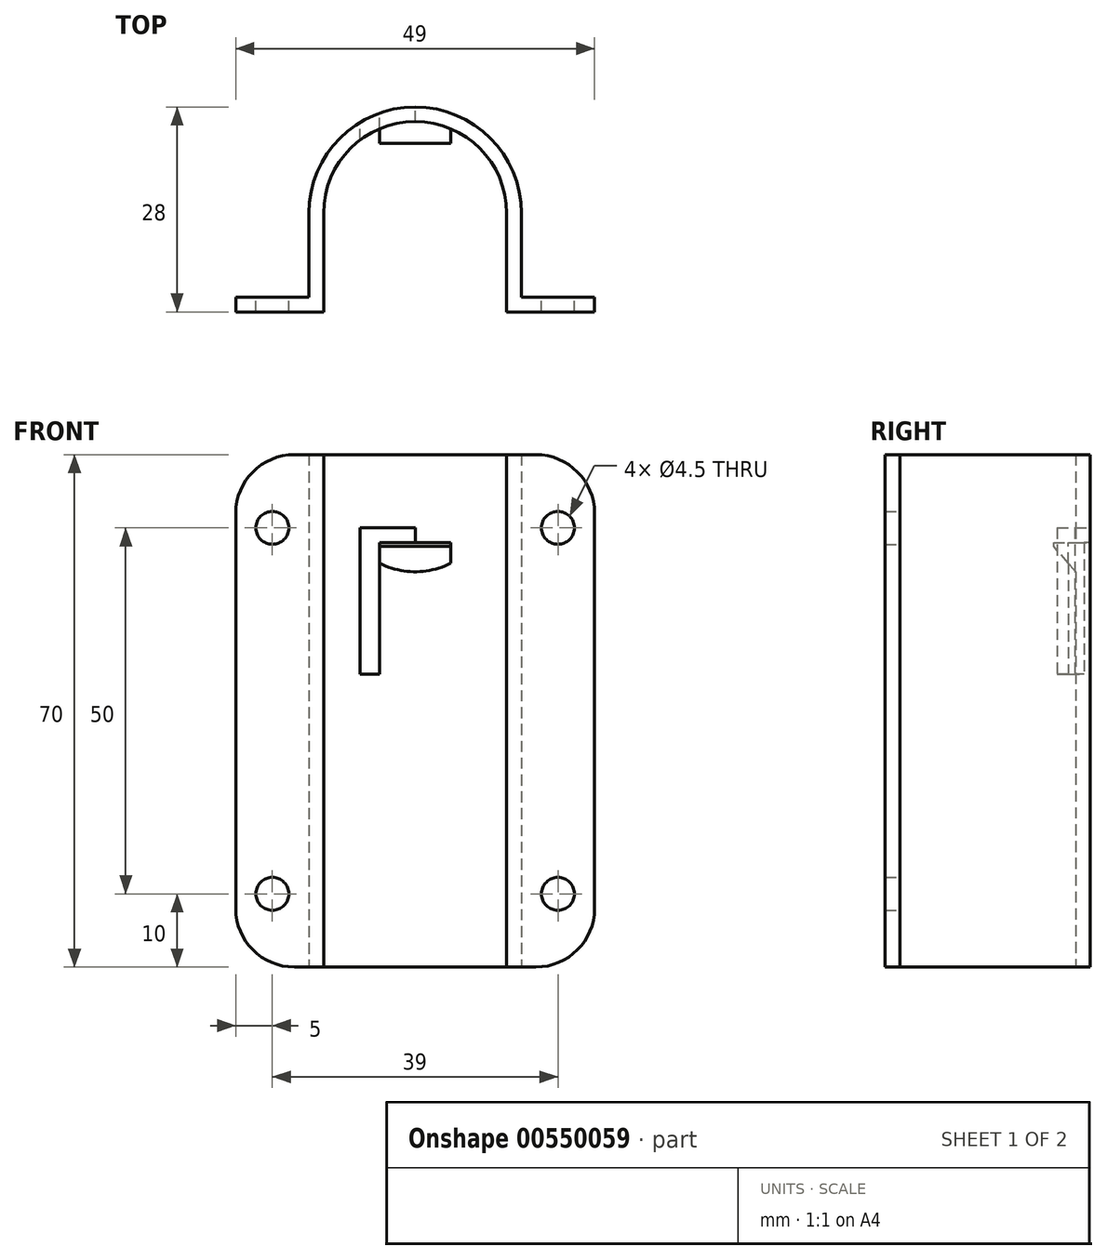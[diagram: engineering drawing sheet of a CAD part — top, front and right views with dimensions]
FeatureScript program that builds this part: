
annotation { "Feature Type Name" : "Feature", "Feature Type Description" : "" }
export const myFeature = defineFeature(function(context is Context, id is Id, definition is map)
    precondition{}
    {
        {
            var Q0;
            Q0=qCreatedBy(makeId("Top.planeOp"),FACE);
            var sketch = newSketch(context, id + "F0", { "sketchPlane" : qUnion([Q0])});
            skLineSegment(sketch, "E0", {"start": v(-24.5, 0) * mm, "end": v(-24.5, 2) * mm});
            skLineSegment(sketch, "E1", {"start": v(-24.5, 2) * mm, "end": v(-14.5, 2) * mm});
            skLineSegment(sketch, "E2", {"start": v(-14.5, 2) * mm, "end": v(-14.5, 13.5) * mm});
            skArc(sketch, "E3", {"start": v(-14.5, 13.5) * mm, "mid": v(-10.25, 23.75) * mm, "end": v(0, 28) * mm});
            skLineSegment(sketch, "E4", {"start": v(0, 28) * mm, "end": v(0, 26) * mm});
            skArc(sketch, "E5", {"start": v(0, 26) * mm, "mid": v(-8.84, 22.34) * mm, "end": v(-12.5, 13.5) * mm});
            skLineSegment(sketch, "E6", {"start": v(-12.5, 13.5) * mm, "end": v(-12.5, 0) * mm});
            skLineSegment(sketch, "E7", {"start": v(-24.5, 0) * mm, "end": v(-12.5, 0) * mm});
            skSolve(sketch);
        }
        {
            var Q0;
            Q0=makeQuery(id+"F0.imprint","IMPRINT",FACE,{"disambiguationData":[TD([[makeQuery(id+"F0.imprint","IMPRINT",EDGE,{"derivedFrom":sQuery(id+"F0.wireOp",EDGE,"E0")}),-1.0]])]});
            extrude(context, id + "F1", {"entities" : qUnion([Q0]), "endBound" : BoundingType.SYMMETRIC, "depth" : 70 * mm, "offsetDistance" : 25 * mm});
        }
        {
            var Q0;
            Q0=makeQuery(id+"F1.opExtrude","SWEPT_FACE",FACE,{"disambiguationData":[OSD([sQuery(id+"F0.wireOp",EDGE,"E1")])]});
            var sketch = newSketch(context, id + "F2", { "sketchPlane" : qUnion([Q0])});
            skPoint(sketch, "E8", {"position": v(19.5, 25) * mm});
            skPoint(sketch, "E9", {"position": v(19.5, -25) * mm});
            skSolve(sketch);
        }
        {
            var Q0;
            Q0=sQuery(id+"F2.wireOp",VERTEX,"E9");
            var Q1;
            Q1=sQuery(id+"F2.wireOp",VERTEX,"E8");
            var Q2;
            Q2=makeQuery(id+"F1.opExtrude","SWEPT_BODY",BODY,{"disambiguationData":[OSD([sQuery(id+"F0.wireOp",EDGE,"E0"),sQuery(id+"F0.wireOp",EDGE,"E1"),sQuery(id+"F0.wireOp",EDGE,"E2"),sQuery(id+"F0.wireOp",EDGE,"E3"),sQuery(id+"F0.wireOp",EDGE,"E4"),sQuery(id+"F0.wireOp",EDGE,"E5"),sQuery(id+"F0.wireOp",EDGE,"E6"),sQuery(id+"F0.wireOp",EDGE,"E7")])]});
            hole(context, id + "F3", {"style" : HoleStyle.SIMPLE, "endStyle" : HoleEndStyle.THROUGH, "holeDiameter" : 4.5 * mm, "isTappedThrough" : true, "tappedDepth" : 12 * mm, "tapClearance" : 3, "locations" : qUnion([Q0, Q1]), "scope" : qUnion([Q2])});
        }
        {
            var Q0;
            Q0=makeQuery(id+"F1.opExtrude","SWEPT_BODY",BODY,{"disambiguationData":[OSD([sQuery(id+"F0.wireOp",EDGE,"E0"),sQuery(id+"F0.wireOp",EDGE,"E1"),sQuery(id+"F0.wireOp",EDGE,"E2"),sQuery(id+"F0.wireOp",EDGE,"E3"),sQuery(id+"F0.wireOp",EDGE,"E4"),sQuery(id+"F0.wireOp",EDGE,"E5"),sQuery(id+"F0.wireOp",EDGE,"E6"),sQuery(id+"F0.wireOp",EDGE,"E7")])]});
            var Q1;
            Q1=qCreatedBy(makeId("Right.planeOp"),FACE);
            mirror(context, id + "F4", {"operationType" : NewBodyOperationType.ADD, "entities" : qUnion([Q0]), "mirrorPlane" : qUnion([Q1])});
        }
        {
            var Q0;
            Q0=qCreatedBy(makeId("Front.planeOp"),FACE);
            cPlane(context, id + "F5", {"entities" : qUnion([Q0]), "cplaneType" : CPlaneType.OFFSET, "offset" : 29 * mm, "oppositeDirection" : true, "width" : 150 * mm, "height" : 150 * mm});
        }
        {
            var Q0;
            Q0=qCreatedBy(id+"F5.planeOp",FACE);
            var sketch = newSketch(context, id + "F6", { "sketchPlane" : qUnion([Q0])});
            skLineSegment(sketch, "E10", {"start": v(0, 25) * mm, "end": v(-7.5, 25) * mm});
            skLineSegment(sketch, "E11", {"start": v(-7.5, 25) * mm, "end": v(-7.5, 5) * mm});
            skLineSegment(sketch, "E12", {"start": v(-7.5, 5) * mm, "end": v(-4.89, 5) * mm});
            skLineSegment(sketch, "E13", {"start": v(-4.89, 5) * mm, "end": v(-4.89, 23) * mm});
            skLineSegment(sketch, "E14", {"start": v(-4.89, 23) * mm, "end": v(0, 23) * mm});
            skLineSegment(sketch, "E15", {"start": v(0, 23) * mm, "end": v(0, 25) * mm});
            skSolve(sketch);
        }
        {
            var Q0;
            Q0=makeQuery(id+"F6.imprint","IMPRINT",FACE,{"disambiguationData":[TD([[makeQuery(id+"F6.imprint","IMPRINT",EDGE,{"derivedFrom":sQuery(id+"F6.wireOp",EDGE,"E10")}),1.0]])]});
            var Q1;
            {var subQ0=makeQuery(id+"F1.opExtrude","SWEPT_FACE",FACE,{"disambiguationData":[OSD([sQuery(id+"F0.wireOp",EDGE,"E5")])]});Q1=makeQuery(id+"F4.boolean.opBoolean","MERGE",FACE,{"derivedFrom":[subQ0,makeQuery(id+"F4.opPattern","COPY",FACE,{"derivedFrom":subQ0,"instanceName":"1"})]});}
            extrude(context, id + "F7", {"entities" : qUnion([Q0]), "operationType" : NewBodyOperationType.REMOVE, "endBound" : BoundingType.UP_TO_SURFACE, "depth" : 25 * mm, "endBoundEntityFace" : qUnion([Q1]), "offsetDistance" : 25 * mm});
        }
        {
            var Q0;
            Q0=makeQuery(id+"F1.opExtrude","CAP_EDGE",EDGE,{"disambiguationData":[OSD([sQuery(id+"F0.wireOp",EDGE,"E0")])],"isStart":true});
            var Q1;
            Q1=makeQuery(id+"F4.opPattern","COPY",EDGE,{"derivedFrom":makeQuery(id+"F1.opExtrude","CAP_EDGE",EDGE,{"disambiguationData":[OSD([sQuery(id+"F0.wireOp",EDGE,"E0")])],"isStart":true}),"instanceName":"1"});
            var Q2;
            Q2=makeQuery(id+"F1.opExtrude","CAP_EDGE",EDGE,{"disambiguationData":[OSD([sQuery(id+"F0.wireOp",EDGE,"E0")])],"isStart":false});
            var Q3;
            Q3=makeQuery(id+"F4.opPattern","COPY",EDGE,{"derivedFrom":makeQuery(id+"F1.opExtrude","CAP_EDGE",EDGE,{"disambiguationData":[OSD([sQuery(id+"F0.wireOp",EDGE,"E0")])],"isStart":false}),"instanceName":"1"});
            fillet(context, id + "F8", {"entities" : qUnion([Q0, Q1, Q2, Q3]), "radius" : 8 * mm, "tangentPropagation" : true, "allowEdgeOverflow" : false});
        }
        {
            var Q0;
            {var subQ0=sQuery(id+"F6.wireOp",EDGE,"E14");Q0=makeQuery(id+"FHmU98y3rWXlE6b_1.1.F7.boolean.opBoolean","MERGE",FACE,{"derivedFrom":[makeQuery(id+"F7.boolean.opBoolean","COPY",FACE,{"derivedFrom":makeQuery(id+"F7.opExtrude","SWEPT_FACE",FACE,{"disambiguationData":[OSD([subQ0])]})}),makeQuery(id+"FHmU98y3rWXlE6b_1.1.F7.opExtrude","SWEPT_FACE",FACE,{"disambiguationData":[OSD([subQ0])]})]});}
            var sketch = newSketch(context, id + "F9", { "sketchPlane" : qUnion([Q0])});
            skLineSegment(sketch, "E16", {"start": v(-4.89, 25) * mm, "end": v(-4.89, 23) * mm});
            skLineSegment(sketch, "E17", {"start": v(-4.89, 23) * mm, "end": v(4.89, 23) * mm});
            skLineSegment(sketch, "E18", {"start": v(4.89, 23) * mm, "end": v(4.89, 25) * mm});
            skArc(sketch, "E19", {"start": v(4.89, 25) * mm, "mid": v(0, 26) * mm, "end": v(-4.89, 25) * mm});
            skSolve(sketch);
        }
        {
            var Q0;
            {var subQ0=sQuery(id+"F9.wireOp",EDGE,"E16");Q0=makeQuery(id+"F9.imprint","IMPRINT",FACE,{"disambiguationData":[TD([[makeQuery(id+"F9.imprint","IMPRINT",EDGE,{"derivedFrom":subQ0}),1.0]])]});}
            extrude(context, id + "F10", {"entities" : qUnion([Q0]), "operationType" : NewBodyOperationType.ADD, "oppositeDirection" : true, "depth" : 4 * mm, "offsetDistance" : 25 * mm});
        }
        {
            var Q0;
            Q0=makeQuery(id+"F10.opExtrude","CAP_EDGE",EDGE,{"disambiguationData":[OSD([sQuery(id+"F9.wireOp",EDGE,"E17")])],"isStart":false});
            chamfer(context, id + "F11", {"entities" : qUnion([Q0]), "chamferType" : ChamferType.TWO_OFFSETS, "width1" : 3 * mm, "oppositeDirection" : true, "width2" : 3.5 * mm, "tangentPropagation" : true});
        }
    });
